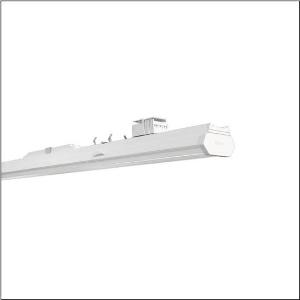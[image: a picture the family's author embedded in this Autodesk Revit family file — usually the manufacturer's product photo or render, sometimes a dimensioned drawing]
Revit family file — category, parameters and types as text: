
# Revit family: licross_r__11_protected_mo_51tp12dn495g3s_1208
name_source: partatom
category: Lighting Fixtures
units: mm (PartAtom-declared; Revit-internal decimal feet)

## family parameters
Cut with Voids When Loaded = No
Host = Face
Light Source = No
Part Type = Normal
Room Calculation Point = No
Round Connector Dimension = Use Diameter
Shared = No

## types (1)
- --- (1 x LED, 980 lm, 6.8 W, 4000K)
    Apparent Load = 7 VA
    CIE Flux Codes = 73 92 98 99 100
    Color Rendering = 80
    Color Temperature = 4000K
    Default Elevation = 1800 mm
    Description = Licross® 11 Protected MO, luminaire insert, of sheet steel, galvanised, coil coated, white, length: 1.500mm, width: 90mm, height: 101mm, LED rated luminous flux: 9.980lm, light colour: 840, control gear: DALI 2 (for two DALI lines), with plug, 6-pole, with phase selection, for trunking rail, 14-core, mains connection: 220..240V, AC, 50/60Hz, rated input power: 61W, for trunking rail, 14-core, halogen-free wiring, for emergency light function, converter,control gear: single battery element, battery: LiFePO4, 9Ah, primary light control with lens, of plastic, primary optical cover: cover, of PMMA, light emission: direct distribution, primary light characteristic: symmetric, protection rating (complete): IP64, insulation class (complete): insulation class I (protective earthing), certification: CE, UKCA, protection symbol: D if used in an environment with conductive dust loads with corresponding accessories, impact resistance: IK06, permissible ambient temperature for indoor applications: +5..+35°C, standard: EN 60598-2-22, LABS conformity tested according to VDMA 24364:2018-05, reducing of maximum allowable ambient temperature of 5°C with ceiling mounting, corresponds to IFS (International Featured Standards) requirements for safety and quality in the food industry, packaging unit: 1 piece
    Height = 92 mm
    Lamp = 1 x LED
    Lamp Light Flux = 980 lm
    Lamp Power = 6.8 W
    Lamp count = 1
    Length = 1500 mm
    Luminous efficacy = 144 lm/W
    Manufacturer = Siteco
    ModVariant = No
    Model = 51TP12DN495G3S
    Mounting Place = Ceiling
    Mounting Type = Pendant
    Number of Poles = 1
    OnlyDefault = Yes
    Power Factor = 1
    Product Name = Licross® 11 Protected MO
    Product group = luminaire insert
    ProductGroupID = 901
    Protection Class = Protection class I
    Protection Degree = IP 64
    RLX_Detail_Level = 1
    RLX_Emergency_Light_Flux = 0 lm
    RLX_Emergency_Type = 0
    RLX_Emergency_Type_DB = No
    RlxData = <blob elided: 24721 chars, md5=766634b5>
    Socket = socket
    Standby Power = 0 W
    System Light Flux = 980 lm
    System Power = 7 W
    Type Comments = : emergency light operation: 3 h
    Type Image = l_1256148.jpg
    URL = http://relux.com
    VarID = @adj_059531
    Voltage = 0 V
    Weight = 0.00 kg
    Width = 88 mm

## geometry (parser evidence)
native form markers: Blend x4, Sweep x11
no freeform markers — native parametric forms only
